FCSTD DOCUMENT  (FreeCAD 0.19R24291 (Git))
Label: Problem 12
License: All rights reserved
LicenseURL: http://en.wikipedia.org/wiki/All_rights_reserved
objects: Part::Part2DObjectPython×39, App::FeaturePython×24
note: 39 computed .brp shape members not serialized (recipe doc carries the construction recipe); baked Part::Feature solids carry a one-line shape summary decoded from their .brp

FEATURE [Part::Part2DObjectPython] Line  # Draft 2D object (typed FeaturePython)
  Area = 0
  ChamferSize = 0
  Closed = false
  End = (88,-7.24598,0)
  FilletRadius = 0
  Length = 88
  MakeFace = false
  Placement = pos=(0,-7.24598,0) rot=(0,0,1;0rad)
  Points = (2) [(0,0,0),(88,2.69422e-15,0)]
  Start = (0,-7.24598,0)
  Subdivisions = 0
FEATURE [Part::Part2DObjectPython] Line002  # Draft 2D object (typed FeaturePython)
  Area = 0
  ChamferSize = 0
  Closed = false
  End = (88,56.754,0)
  FilletRadius = 0
  Length = 88
  MakeFace = false
  Placement = pos=(0,-7.24598,0) rot=(0,0,1;0rad)
  Points = (2) [(-3.91887e-15,64,0),(88,64,0)]
  Start = (-3.9e-15,56.754,0)
  Subdivisions = 0
FEATURE [Part::Part2DObjectPython] Line003  # Draft 2D object (typed FeaturePython)
  Area = 0
  ChamferSize = 0
  Closed = false
  End = (88,105.851,0)
  FilletRadius = 0
  Length = 24
  MakeFace = false
  Placement = pos=(88,64,0) rot=(0,0,1;0rad)
  Points = (2) [(0,65.8507,0),(0,41.8507,0)]
  Start = (88,129.851,0)
  Subdivisions = 0
FEATURE [Part::Part2DObjectPython] Line006  # Draft 2D object (typed FeaturePython)
  Area = 0
  ChamferSize = 0
  Closed = false
  End = (76,44.754,0)
  FilletRadius = 0
  Length = 12
  MakeFace = false
  Placement = pos=(0,-7.24598,0) rot=(0,0,1;0rad)
  Points = (2) [(76,64,0),(76,52,0)]
  Start = (76,56.754,0)
  Subdivisions = 0
FEATURE [Part::Part2DObjectPython] Arc  # Draft 2D object (typed FeaturePython)
  Area = 0
  FirstAngle = -270
  LastAngle = -90
  MakeFace = false
  Placement = pos=(76,24.754,0) rot=(0,0,1;0rad)
  Radius = 20
FEATURE [Part::Part2DObjectPython] Line008  # Draft 2D object (typed FeaturePython)
  Area = 0
  ChamferSize = 0
  Closed = false
  End = (0,36.754,0)
  FilletRadius = 0
  Length = 44
  MakeFace = false
  Placement = pos=(44,36.754,0) rot=(0,0,1;0rad)
  Points = (2) [(0,0,0),(-44,0,0)]
  Start = (44,36.754,0)
  Subdivisions = 0
FEATURE [Part::Part2DObjectPython] Line011  # Draft 2D object (typed FeaturePython)
  Area = 0
  ChamferSize = 0
  Closed = false
  End = (0,105.851,0)
  FilletRadius = 0
  Length = 108
  MakeFace = false
  Points = (2) [(108,105.851,0),(0,105.851,0)]
  Start = (108,105.851,0)
  Subdivisions = 0
FEATURE [Part::Part2DObjectPython] Line012  # Draft 2D object (typed FeaturePython)
  Area = 0
  ChamferSize = 0
  Closed = false
  End = (0,161.851,0)
  FilletRadius = 0
  Length = 56
  MakeFace = false
  Placement = pos=(0,105.851,0) rot=(0,0,1;0rad)
  Points = (2) [(0,0,0),(1.71451e-15,56,0)]
  Start = (0,105.851,0)
  Subdivisions = 0
FEATURE [Part::Part2DObjectPython] Line013  # Draft 2D object (typed FeaturePython)
  Area = 0
  ChamferSize = 0
  Closed = false
  End = (44,161.851,0)
  FilletRadius = 0
  Length = 44
  MakeFace = false
  Points = (2) [(44,117.851,0),(44,161.851,0)]
  Start = (44,117.851,0)
  Subdivisions = 0
FEATURE [Part::Part2DObjectPython] Line014  # Draft 2D object (typed FeaturePython)
  Area = 0
  ChamferSize = 0
  Closed = false
  End = (76,161.851,0)
  FilletRadius = 0
  Length = 32
  MakeFace = false
  Placement = pos=(0,24,0) rot=(0,0,1;0rad)
  Points = (2) [(76,105.851,0),(76,137.851,0)]
  Start = (76,129.851,0)
  Subdivisions = 0
FEATURE [Part::Part2DObjectPython] Line015  # Draft 2D object (typed FeaturePython)
  Area = 0
  ChamferSize = 0
  Closed = false
  End = (56,161.851,0)
  FilletRadius = 0
  Length = 32
  MakeFace = false
  Placement = pos=(0,24,0) rot=(0,0,1;0rad)
  Points = (2) [(56,105.851,0),(56,137.851,0)]
  Start = (56,129.851,0)
  Subdivisions = 0
FEATURE [Part::Part2DObjectPython] Line017  # Draft 2D object (typed FeaturePython)
  Area = 0
  ChamferSize = 0
  Closed = false
  End = (76,161.851,0)
  FilletRadius = 0
  Length = 76
  MakeFace = false
  Placement = pos=(0,161.851,0) rot=(0,0,1;0rad)
  Points = (2) [(0,0,0),(76,0,0)]
  Start = (0,161.851,0)
  Subdivisions = 0
FEATURE [Part::Part2DObjectPython] Line018  # Draft 2D object (typed FeaturePython)
  Area = 0
  ChamferSize = 0
  Closed = false
  End = (76,129.851,0)
  FilletRadius = 0
  Length = 18
  MakeFace = false
  Placement = pos=(56,129.851,0) rot=(0,0,1;0rad)
  Points = (2) [(38,0,0),(20,0,0)]
  Start = (94,129.851,0)
  Subdivisions = 0
FEATURE [Part::Part2DObjectPython] Line021  # Draft 2D object (typed FeaturePython)
  Area = 0
  ChamferSize = 0
  Closed = false
  End = (94,129.851,0)
  FilletRadius = 0
  Length = 27.7849
  MakeFace = false
  Placement = pos=(108,105.851,0) rot=(0,0,1;0rad)
  Points = (2) [(0,0,0),(-14,24,0)]
  Start = (108,105.851,0)
  Subdivisions = 0
FEATURE [Part::Part2DObjectPython] Line023  # Draft 2D object (typed FeaturePython)
  Area = 0
  ChamferSize = 0
  Closed = false
  End = (88,36.754,0)
  FilletRadius = 0
  Length = 20
  MakeFace = false
  Placement = pos=(0,-7.24598,0) rot=(0,0,1;0rad)
  Points = (2) [(108,44,0),(88,44,0)]
  Start = (108,36.754,0)
  Subdivisions = 0
FEATURE [Part::Part2DObjectPython] Line024  # Draft 2D object (typed FeaturePython)
  Area = 0
  ChamferSize = 0
  Closed = true
  End = (88,12.754,0)
  FilletRadius = 0
  Length = 20
  MakeFace = false
  Placement = pos=(88,56.754,0) rot=(0,0,1;0rad)
  Points = (2) [(0,-44,0),(0,-44,0)]
  Start = (88,12.754,0)
  Subdivisions = 0
FEATURE [Part::Part2DObjectPython] Line026  # Draft 2D object (typed FeaturePython)
  Area = 0
  ChamferSize = 0
  Closed = false
  End = (94,24.754,0)
  FilletRadius = 0
  Length = 12
  MakeFace = false
  Placement = pos=(0,-7.24598,0) rot=(0,0,1;0rad)
  Points = (2) [(94,44,0),(94,32,0)]
  Start = (94,36.754,0)
  Subdivisions = 0
FEATURE [Part::Part2DObjectPython] Line028  # Draft 2D object (typed FeaturePython)
  Area = 0
  ChamferSize = 0
  Closed = false
  End = (88,12.754,0)
  FilletRadius = 0
  Length = 20
  MakeFace = false
  Placement = pos=(0,-7.24598,0) rot=(0,0,1;0rad)
  Points = (2) [(108,20,0),(88,20,0)]
  Start = (108,12.754,0)
  Subdivisions = 0
FEATURE [Part::Part2DObjectPython] Line029  # Draft 2D object (typed FeaturePython)
  Area = 0
  ChamferSize = 0
  Closed = false
  End = (94,12.754,0)
  FilletRadius = 0
  Length = 12
  MakeFace = false
  Placement = pos=(0,-7.24598,0) rot=(0,0,1;0rad)
  Points = (2) [(94,32,0),(94,20,0)]
  Start = (94,24.754,0)
  Subdivisions = 0
FEATURE [Part::Part2DObjectPython] Line030  # Draft 2D object (typed FeaturePython)
  Area = 0
  ChamferSize = 0
  Closed = false
  End = (76,24.754,0)
  FilletRadius = 0
  Length = 18
  MakeFace = false
  Placement = pos=(94,24.754,0) rot=(0,0,1;0rad)
  Points = (2) [(0,0,0),(-18,0,0)]
  Start = (94,24.754,0)
  Subdivisions = 0
FEATURE [Part::Part2DObjectPython] Line031  # Draft 2D object (typed FeaturePython)
  Area = 0
  ChamferSize = 0
  Closed = false
  End = (76,4.75402,0)
  FilletRadius = 0
  Length = 40
  MakeFace = false
  Placement = pos=(0,-7.24598,0) rot=(0,0,1;0rad)
  Points = (2) [(76,52,0),(76,12,0)]
  Start = (76,44.754,0)
  Subdivisions = 0
FEATURE [Part::Part2DObjectPython] Line032  # Draft 2D object (typed FeaturePython)
  Area = 0
  ChamferSize = 0
  Closed = false
  End = (76,-7.24598,0)
  FilletRadius = 0
  Length = 12
  MakeFace = false
  Placement = pos=(0,-7.24598,0) rot=(0,0,1;0rad)
  Points = (2) [(76,12,0),(76,7.10543e-15,0)]
  Start = (76,4.75402,0)
  Subdivisions = 0
FEATURE [Part::Part2DObjectPython] Line033  # Draft 2D object (typed FeaturePython)
  Area = 0
  ChamferSize = 0
  Closed = false
  End = (-82.7769,129.851,0)
  FilletRadius = 0
  Length = 12
  MakeFace = false
  Placement = pos=(106.727,129.851,0) rot=(0,0,1;0rad)
  Points = (2) [(-201.503,0,0),(-189.503,0,0)]
  Start = (-94.7769,129.851,0)
  Subdivisions = 0
FEATURE [Part::Part2DObjectPython] Line034  # Draft 2D object (typed FeaturePython)
  Area = 0
  ChamferSize = 0
  Closed = false
  End = (-94.7769,161.851,0)
  FilletRadius = 0
  Length = 56
  MakeFace = false
  Placement = pos=(50.7266,0,0) rot=(0,0,1;0rad)
  Points = (2) [(-145.503,105.851,0),(-145.503,161.851,0)]
  Start = (-94.7769,105.851,0)
  Subdivisions = 0
FEATURE [Part::Part2DObjectPython] Line035  # Draft 2D object (typed FeaturePython)
  Area = 0
  ChamferSize = 0
  Closed = false
  End = (-30.7769,161.851,0)
  FilletRadius = 0
  Length = 56
  MakeFace = false
  Placement = pos=(50.7266,0,0) rot=(0,0,1;0rad)
  Points = (2) [(-81.5035,105.851,0),(-81.5035,161.851,0)]
  Start = (-30.7769,105.851,0)
  Subdivisions = 0
FEATURE [Part::Part2DObjectPython] Line036  # Draft 2D object (typed FeaturePython)
  Area = 0
  ChamferSize = 0
  Closed = false
  End = (-30.7769,105.851,0)
  FilletRadius = 0
  Length = 64
  MakeFace = false
  Placement = pos=(-94.7769,105.851,0) rot=(0,0,1;0rad)
  Points = (2) [(0,0,0),(64,0,0)]
  Start = (-94.7769,105.851,0)
  Subdivisions = 0
FEATURE [Part::Part2DObjectPython] Line037  # Draft 2D object (typed FeaturePython)
  Area = 0
  ChamferSize = 0
  Closed = false
  End = (-94.7769,161.851,0)
  FilletRadius = 0
  Length = 64
  MakeFace = false
  Placement = pos=(-30.7769,161.851,0) rot=(0,0,1;0rad)
  Points = (2) [(0,0,0),(-64,0,0)]
  Start = (-30.7769,161.851,0)
  Subdivisions = 0
FEATURE [Part::Part2DObjectPython] Line040  # Draft 2D object (typed FeaturePython)
  Area = 0
  ChamferSize = 0
  Closed = false
  End = (76,129.851,0)
  FilletRadius = 0
  Length = 20
  MakeFace = false
  Placement = pos=(56,129.851,0) rot=(0,0,1;0rad)
  Points = (2) [(0,0,0),(20,0,0)]
  Start = (56,129.851,0)
  Subdivisions = 0
FEATURE [Part::Part2DObjectPython] Line041  # Draft 2D object (typed FeaturePython)
  Area = 0
  ChamferSize = 0
  Closed = false
  End = (-30.7769,129.851,0)
  FilletRadius = 0
  Length = 52
  MakeFace = false
  Placement = pos=(106.727,129.851,0) rot=(0,0,1;0rad)
  Points = (2) [(-189.503,0,0),(-137.503,0,0)]
  Start = (-82.7769,129.851,0)
  Subdivisions = 0
FEATURE [Part::Part2DObjectPython] Line042  # Draft 2D object (typed FeaturePython)
  Area = 0
  ChamferSize = 0
  Closed = false
  End = (-82.7769,161.851,0)
  FilletRadius = 0
  Length = 32
  MakeFace = false
  Placement = pos=(-82.7769,129.851,0) rot=(0,0,1;0rad)
  Points = (2) [(0,0,0),(0,32,0)]
  Start = (-82.7769,129.851,0)
  Subdivisions = 0
FEATURE [Part::Part2DObjectPython] Line043  # Draft 2D object (typed FeaturePython)
  Area = 0
  ChamferSize = 0
  Closed = false
  End = (-42.7769,161.851,0)
  FilletRadius = 0
  Length = 32
  MakeFace = false
  Placement = pos=(50.7266,0,0) rot=(0,0,1;0rad)
  Points = (2) [(-93.5035,129.851,0),(-93.5035,161.851,0)]
  Start = (-42.7769,129.851,0)
  Subdivisions = 0
FEATURE [Part::Part2DObjectPython] Line044  # Draft 2D object (typed FeaturePython)
  Area = 0
  ChamferSize = 0
  Closed = false
  End = (-50.7769,129.851,0)
  FilletRadius = 0
  Length = 24
  MakeFace = false
  Placement = pos=(50.7266,0,0) rot=(0,0,1;0rad)
  Points = (2) [(-101.503,105.851,0),(-101.503,129.851,0)]
  Start = (-50.7769,105.851,0)
  Subdivisions = 0
FEATURE [Part::Part2DObjectPython] Line045  # Draft 2D object (typed FeaturePython)
  Area = 0
  ChamferSize = 0
  Closed = false
  End = (-74.7769,129.851,0)
  FilletRadius = 0
  Length = 24
  MakeFace = false
  Placement = pos=(50.7266,0,0) rot=(0,0,1;0rad)
  Points = (2) [(-125.503,105.851,0),(-125.503,129.851,0)]
  Start = (-74.7769,105.851,0)
  Subdivisions = 0
FEATURE [Part::Part2DObjectPython] Arc001  # Draft 2D object (typed FeaturePython)
  Area = 0
  FirstAngle = -90
  LastAngle = 0
  MakeFace = false
  Placement = pos=(-94.7769,161.851,0) rot=(0,0,1;0rad)
  Radius = 44
FEATURE [Part::Part2DObjectPython] Line046  # Draft 2D object (typed FeaturePython)
  Area = 0
  ChamferSize = 0
  Closed = false
  End = (0,117.851,0)
  FilletRadius = 0
  Length = 44
  MakeFace = false
  Placement = pos=(44,117.851,0) rot=(0,0,1;0rad)
  Points = (2) [(0,0,0),(-44,0,0)]
  Start = (44,117.851,0)
  Subdivisions = 0
FEATURE [App::FeaturePython] Dimension  # Draft dimension (typed FeaturePython)
  Diameter = false
  Dimline = (-82.7769,169.851,0)
  Direction = (0,0,0)
  Distance = 12
  End = (-82.7769,161.851,0)
  Normal = (0,0,1)
  Start = (-94.7769,161.851,0)
FEATURE [App::FeaturePython] Dimension001  # Draft dimension (typed FeaturePython)
  Diameter = false
  Dimline = (-42.7769,169.851,0)
  Direction = (0,0,0)
  Distance = 40
  End = (-42.7769,161.851,0)
  Normal = (0,0,1)
  Start = (-82.7769,161.851,0)
FEATURE [App::FeaturePython] Dimension002  # Draft dimension (typed FeaturePython)
  Diameter = false
  Dimline = (-42.7769,169.832,0)
  Direction = (0,0,0)
  Distance = 12
  End = (-42.7769,161.851,0)
  Normal = (0,0,1)
  Start = (-30.7769,161.851,0)
FEATURE [App::FeaturePython] Dimension003  # Draft dimension (typed FeaturePython)
  Diameter = false
  Dimline = (-83.2772,169.334,0)
  Direction = (0,0,0)
  Distance = 76
  End = (76,161.851,0)
  Normal = (0,0,1)
  Start = (0,161.851,0)
FEATURE [App::FeaturePython] Dimension004  # Draft dimension (typed FeaturePython)
  Diameter = false
  Dimline = (-111.459,109.343,0)
  Direction = (0,0,0)
  Distance = 56
  End = (-94.7769,105.851,0)
  Normal = (0,0,1)
  Start = (-94.7769,161.851,0)
FEATURE [App::FeaturePython] Dimension005  # Draft dimension (typed FeaturePython)
  Diameter = false
  Dimline = (-7.60451,105.851,0)
  Direction = (0,0,0)
  Distance = 12
  End = (0,105.851,0)
  Normal = (0,0,1)
  Start = (0,117.851,0)
FEATURE [App::FeaturePython] Dimension006  # Draft dimension (typed FeaturePython)
  Diameter = false
  Dimline = (125.628,116.321,0)
  Direction = (0,0,0)
  Distance = 32
  End = (76,129.851,0)
  Normal = (0,0,1)
  Start = (76,161.851,0)
FEATURE [App::FeaturePython] Dimension007  # Draft dimension (typed FeaturePython)
  Diameter = false
  Dimline = (125.379,133.248,0)
  Direction = (0,0,0)
  Distance = 24
  End = (88,105.851,0)
  Normal = (0,0,1)
  Start = (88,129.851,0)
FEATURE [App::FeaturePython] Dimension008  # Draft dimension (typed FeaturePython)
  Diameter = false
  Dimline = (94,43.7835,0)
  Direction = (0,0,0)
  Distance = 6
  End = (94,36.754,0)
  Normal = (0,0,1)
  Start = (88,36.754,0)
FEATURE [App::FeaturePython] Dimension009  # Draft dimension (typed FeaturePython)
  Diameter = false
  Dimline = (-7.04741,107.259,0)
  Direction = (0,0,0)
  Distance = 20
  End = (0,56.754,0)
  Normal = (0,0,1)
  Start = (0,36.754,0)
FEATURE [App::FeaturePython] Dimension010  # Draft dimension (typed FeaturePython)
  Diameter = false
  Dimline = (-18.7468,-3.51192,0)
  Direction = (0,0,0)
  Distance = 64
  End = (0,-7.24598,0)
  Normal = (0,0,1)
  Start = (-2e-15,56.754,0)
FEATURE [App::FeaturePython] Dimension011  # Draft dimension (typed FeaturePython)
  Diameter = false
  Dimline = (-82.7769,97.8507,0)
  Direction = (0,0,0)
  Distance = 20
  End = (-74.7769,105.851,0)
  Normal = (0,0,1)
  Start = (-94.7769,105.851,0)
FEATURE [App::FeaturePython] Dimension012  # Draft dimension (typed FeaturePython)
  Diameter = false
  Dimline = (-58.7769,97.8507,0)
  Direction = (0,0,0)
  Distance = 24
  End = (-50.7769,105.851,0)
  Normal = (0,0,1)
  Start = (-74.7769,105.851,0)
FEATURE [App::FeaturePython] Dimension013  # Draft dimension (typed FeaturePython)
  Diameter = false
  Dimline = (45.7,97.8507,0)
  Direction = (0,0,0)
  Distance = 88
  End = (88,105.851,0)
  Normal = (0,0,1)
  Start = (0,105.851,0)
FEATURE [App::FeaturePython] Dimension014  # Draft dimension (typed FeaturePython)
  Diameter = false
  Dimline = (-30.7769,88.8507,0)
  Direction = (0,0,0)
  Distance = 64
  End = (-30.7769,105.851,0)
  Normal = (0,0,1)
  Start = (-94.7769,105.851,0)
FEATURE [App::FeaturePython] Dimension015  # Draft dimension (typed FeaturePython)
  Diameter = false
  Dimline = (108,88.8507,0)
  Direction = (0,0,0)
  Distance = 108
  End = (108,105.851,0)
  Normal = (0,0,1)
  Start = (0,105.851,0)
FEATURE [App::FeaturePython] Dimension016  # Draft dimension (typed FeaturePython)
  Diameter = false
  Dimline = (44,62.754,0)
  Direction = (0,0,0)
  Distance = 44
  End = (44,56.754,0)
  Normal = (0,0,1)
  Start = (-2e-15,56.754,0)
FEATURE [App::FeaturePython] Dimension017  # Draft dimension (typed FeaturePython)
  Diameter = false
  Dimline = (76,62.754,0)
  Direction = (0,0,0)
  Distance = 32
  End = (76,56.754,0)
  Normal = (0,0,1)
  Start = (44,56.754,0)
FEATURE [App::FeaturePython] Dimension018  # Draft dimension (typed FeaturePython)
  Diameter = false
  Dimline = (88,62.754,0)
  Direction = (0,0,0)
  Distance = 12
  End = (88,56.754,0)
  Normal = (0,0,1)
  Start = (76,56.754,0)
FEATURE [Part::Part2DObjectPython] Line047  # Draft 2D object (typed FeaturePython)
  Area = 0
  ChamferSize = 0
  Closed = false
  End = (108,12.754,0)
  FilletRadius = 0
  Length = 24
  MakeFace = false
  Placement = pos=(108,36.754,0) rot=(0,0,1;0rad)
  Points = (2) [(0,0,0),(0,-24,0)]
  Start = (108,36.754,0)
  Subdivisions = 0
FEATURE [Part::Part2DObjectPython] Line048  # Draft 2D object (typed FeaturePython)
  Area = 0
  ChamferSize = 0
  Closed = false
  End = (0,-7.24598,0)
  FilletRadius = 0
  Length = 64
  MakeFace = false
  Placement = pos=(-3.9e-15,56.754,0) rot=(0,0,1;0rad)
  Points = (2) [(0,0,0),(1.95943e-15,-64,0)]
  Start = (-3.9e-15,56.754,0)
  Subdivisions = 0
FEATURE [Part::Part2DObjectPython] Line049  # Draft 2D object (typed FeaturePython)
  Area = 0
  ChamferSize = 0
  Closed = false
  End = (44,-7.24598,0)
  FilletRadius = 0
  Length = 44
  MakeFace = false
  Placement = pos=(44,36.754,0) rot=(0,0,1;0rad)
  Points = (2) [(0,0,0),(7.10543e-15,-44,0)]
  Start = (44,36.754,0)
  Subdivisions = 0
FEATURE [App::FeaturePython] Text  # WARN: FeaturePython — macro-defined, semantics opaque (R4)
  Placement = pos=(-88.4271,74.6765,0) rot=(0,0,1;0rad)
  Text = RIGHT SIDE VIEW
FEATURE [App::FeaturePython] Text001  # WARN: FeaturePython — macro-defined, semantics opaque (R4)
  Placement = pos=(40.2662,74.1787,0) rot=(0,0,1;0rad)
  Text = FRONT VIEW
FEATURE [App::FeaturePython] Text002  # WARN: FeaturePython — macro-defined, semantics opaque (R4)
  Placement = pos=(36.2844,-32.1824,0) rot=(0,0,1;0rad)
  Text = TOP VIEW
FEATURE [App::FeaturePython] Text003  # WARN: FeaturePython — macro-defined, semantics opaque (R4)
  Placement = pos=(-45.6401,-41.6309,0) rot=(0,0,1;0rad)
  Text = ALL DIMENSIONS ARE IN mm
FEATURE [App::FeaturePython] dLabel  # WARN: FeaturePython — macro-defined, semantics opaque (R4)
  CustomText = R20
  LabelType = 0
  Placement = pos=(71.3593,-14.0294,0) rot=(0,0,1;0rad)
  Points = (3) [(71.3593,-14.0294,0),(56.412,-14.0294,0),(63.3217,9.09407,0)]
  StraightDirection = 0
  StraightDistance = -14.9473
  TargetPoint = (63.3217,9.09407,0)
  Text = R20
FEATURE [Part::Part2DObjectPython] Line050  # Draft 2D object (typed FeaturePython)
  Area = 0
  ChamferSize = 0
  Closed = false
  End = (88,56.754,0)
  FilletRadius = 0
  Length = 20
  MakeFace = false
  Placement = pos=(88,36.754,0) rot=(0,0,1;0rad)
  Points = (2) [(0,0,0),(0,20,0)]
  Start = (88,36.754,0)
  Subdivisions = 0
